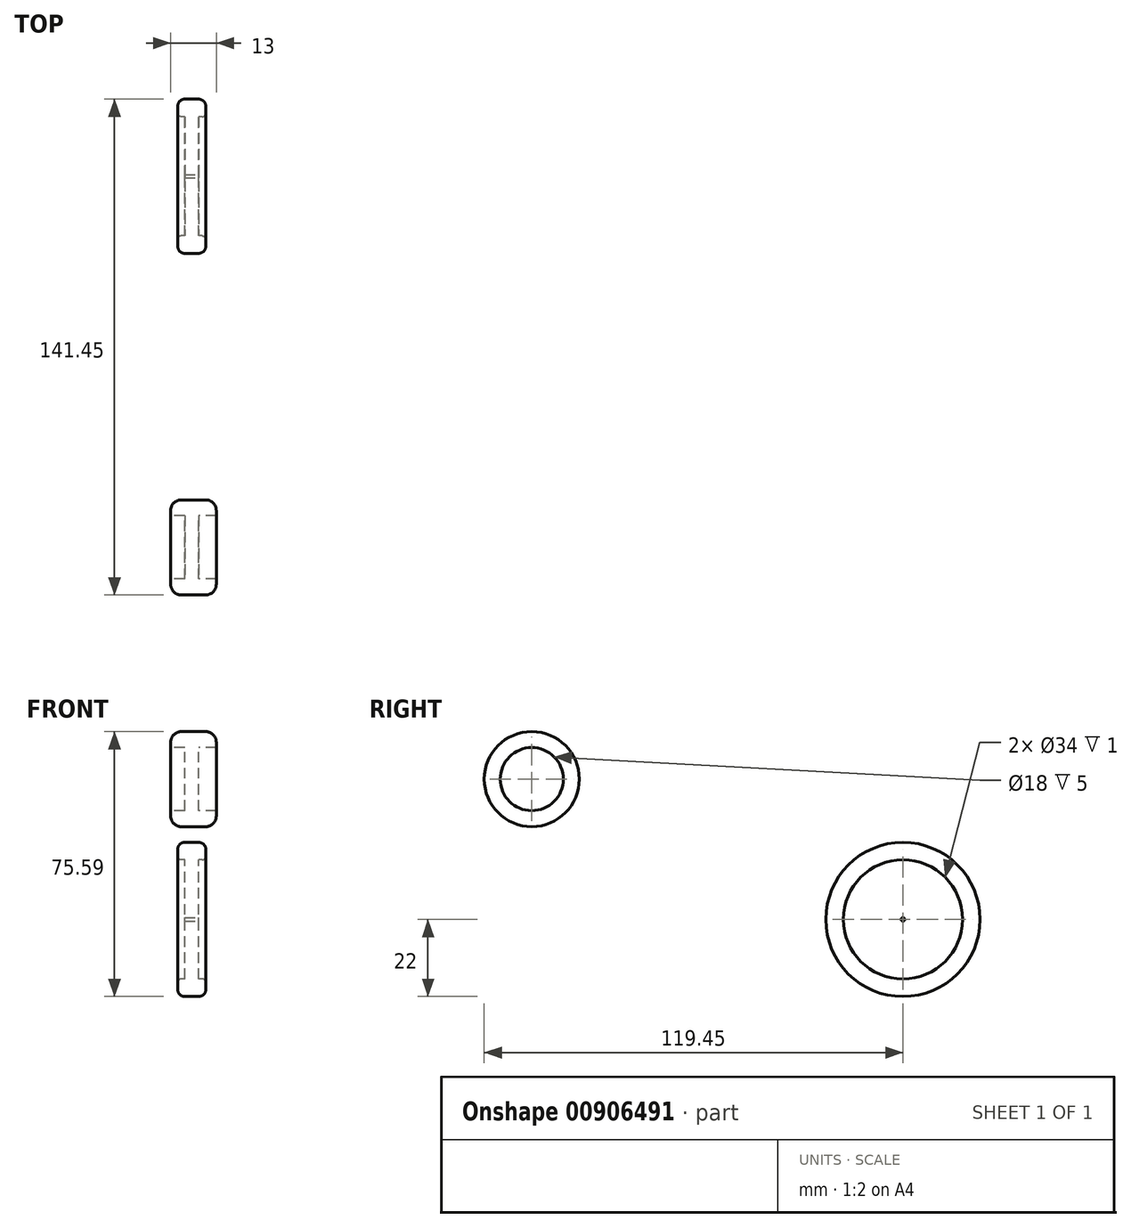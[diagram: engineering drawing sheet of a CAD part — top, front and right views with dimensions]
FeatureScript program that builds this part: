
annotation { "Feature Type Name" : "Feature", "Feature Type Description" : "" }
export const myFeature = defineFeature(function(context is Context, id is Id, definition is map)
    precondition{}
    {
        {
            var Q0;
            Q0=qCreatedBy(makeId("Right.planeOp"),FACE);
            var sketch = newSketch(context, id + "F0", { "sketchPlane" : qUnion([Q0])});
            skCircle(sketch, "E0", {"center": v(0, 0) * mm, "radius": 22 * mm});
            skCircle(sketch, "E1.0", {"center": v(0, 0) * mm, "radius": 17 * mm});
            skSolve(sketch);
        }
        {
            var Q0;
            Q0=makeQuery(id+"F0.imprint","IMPRINT",FACE,{"disambiguationData":[TD([[makeQuery(id+"F0.imprint","IMPRINT",EDGE,{"derivedFrom":sQuery(id+"F0.wireOp",EDGE,"E1.0")}),1.0]])]});
            extrude(context, id + "F1", {"entities" : qUnion([Q0]), "depth" : 2 * mm, "offsetDistance" : 25 * mm, "hasSecondDirection" : true, "secondDirectionOppositeDirection" : true, "secondDirectionDepth" : 2 * mm});
        }
        {
            var Q0;
            Q0=makeQuery(id+"F0.imprint","IMPRINT",FACE,{"disambiguationData":[TD([[makeQuery(id+"F0.imprint","IMPRINT",EDGE,{"derivedFrom":sQuery(id+"F0.wireOp",EDGE,"E0")}),1.0]])]});
            extrude(context, id + "F2", {"entities" : qUnion([Q0]), "operationType" : NewBodyOperationType.ADD, "depth" : 4 * mm, "offsetDistance" : 25 * mm, "hasSecondDirection" : true, "secondDirectionOppositeDirection" : true, "secondDirectionDepth" : 4 * mm});
        }
        {
            var Q0;
            Q0=makeQuery(id+"F2.opExtrude","CAP_EDGE",EDGE,{"disambiguationData":[OSD([sQuery(id+"F0.wireOp",EDGE,"E0")])],"isStart":false});
            var Q1;
            Q1=makeQuery(id+"F2.opExtrude","CAP_EDGE",EDGE,{"disambiguationData":[OSD([sQuery(id+"F0.wireOp",EDGE,"E0")])],"isStart":true});
            fillet(context, id + "F3", {"entities" : qUnion([Q0, Q1]), "radius" : 2 * mm, "tangentPropagation" : true, "allowEdgeOverflow" : false});
        }
        {
            var Q0;
            Q0=makeQuery(id+"F2.opExtrude","CAP_EDGE",EDGE,{"disambiguationData":[OSD([sQuery(id+"F0.wireOp",EDGE,"E1.0")])],"isStart":false});
            var Q1;
            Q1=makeQuery(id+"F2.opExtrude","CAP_EDGE",EDGE,{"disambiguationData":[OSD([sQuery(id+"F0.wireOp",EDGE,"E1.0")])],"isStart":true});
            fillet(context, id + "F4", {"entities" : qUnion([Q0, Q1]), "radius" : 1 * mm, "tangentPropagation" : true, "allowEdgeOverflow" : false});
        }
        {
            var Q0;
            Q0=makeQuery(id+"F1.opExtrude","CAP_FACE",FACE,{"disambiguationData":[OSD([sQuery(id+"F0.wireOp",EDGE,"E1.0")])],"isStart":false});
            var sketch = newSketch(context, id + "F5", { "sketchPlane" : qUnion([Q0])});
            skCircle(sketch, "E2", {"center": v(0, 0) * mm, "radius": 0.5 * mm});
            skSolve(sketch);
        }
        {
            var Q0;
            Q0=makeQuery(id+"F5.imprint","IMPRINT",FACE,{"disambiguationData":[TD([[makeQuery(id+"F5.imprint","IMPRINT",EDGE,{"derivedFrom":sQuery(id+"F5.wireOp",EDGE,"E2")}),1.0]])]});
            extrude(context, id + "F6", {"entities" : qUnion([Q0]), "operationType" : NewBodyOperationType.REMOVE, "oppositeDirection" : true, "depth" : 25 * mm, "offsetDistance" : 25 * mm, "hasSecondDirection" : true, "secondDirectionOppositeDirection" : false, "secondDirectionDepth" : 25 * mm});
        }
        {
            var Q0;
            Q0=qCreatedBy(makeId("Right.planeOp"),FACE);
            var sketch = newSketch(context, id + "F7", { "sketchPlane" : qUnion([Q0])});
            skCircle(sketch, "E3", {"center": v(-105.89, 40.03) * mm, "radius": 14 * mm});
            skCircle(sketch, "E4.0", {"center": v(-105.89, 40.03) * mm, "radius": 9 * mm});
            skCircle(sketch, "E5", {"center": v(-105.89, 40.03) * mm, "radius": 9.02 * mm});
            skSolve(sketch);
        }
        {
            var Q0;
            Q0=makeQuery(id+"F7.imprint","IMPRINT",FACE,{"disambiguationData":[TD([[makeQuery(id+"F7.imprint","IMPRINT",EDGE,{"derivedFrom":sQuery(id+"F7.wireOp",EDGE,"E4.0")}),1.0]])]});
            extrude(context, id + "F8", {"entities" : qUnion([Q0]), "depth" : 2 * mm, "offsetDistance" : 25 * mm, "hasSecondDirection" : true, "secondDirectionOppositeDirection" : true, "secondDirectionDepth" : 2 * mm});
        }
        {
            var Q0;
            Q0=makeQuery(id+"F8.opExtrude","CAP_FACE",FACE,{"disambiguationData":[OSD([sQuery(id+"F7.wireOp",EDGE,"E4.0")])],"isStart":false});
            var sketch = newSketch(context, id + "F9", { "sketchPlane" : qUnion([Q0])});
            skCircle(sketch, "E6", {"center": v(-105.89, 40.03) * mm, "radius": 13.56 * mm});
            skSolve(sketch);
        }
        {
            var Q0;
            Q0=makeQuery(id+"F9.imprint","IMPRINT",FACE,{"disambiguationData":[TD([[makeQuery(id+"F9.imprint","IMPRINT",EDGE,{"derivedFrom":sQuery(id+"F9.wireOp",EDGE,"E6")}),1.0]])]});
            extrude(context, id + "F10", {"entities" : qUnion([Q0]), "operationType" : NewBodyOperationType.ADD, "depth" : 5 * mm, "offsetDistance" : 25 * mm, "hasSecondDirection" : true, "secondDirectionOppositeDirection" : true, "secondDirectionDepth" : 8 * mm});
        }
        {
            var Q0;
            Q0=makeQuery(id+"F10.opExtrude","CAP_EDGE",EDGE,{"disambiguationData":[OSD([sQuery(id+"F9.wireOp",EDGE,"E6")])],"isStart":false});
            var Q1;
            Q1=makeQuery(id+"F10.opExtrude","CAP_EDGE",EDGE,{"disambiguationData":[OSD([sQuery(id+"F9.wireOp",EDGE,"E6")])],"isStart":true});
            fillet(context, id + "F11", {"entities" : qUnion([Q0, Q1]), "radius" : 3 * mm, "tangentPropagation" : true, "allowEdgeOverflow" : false});
        }
    });
